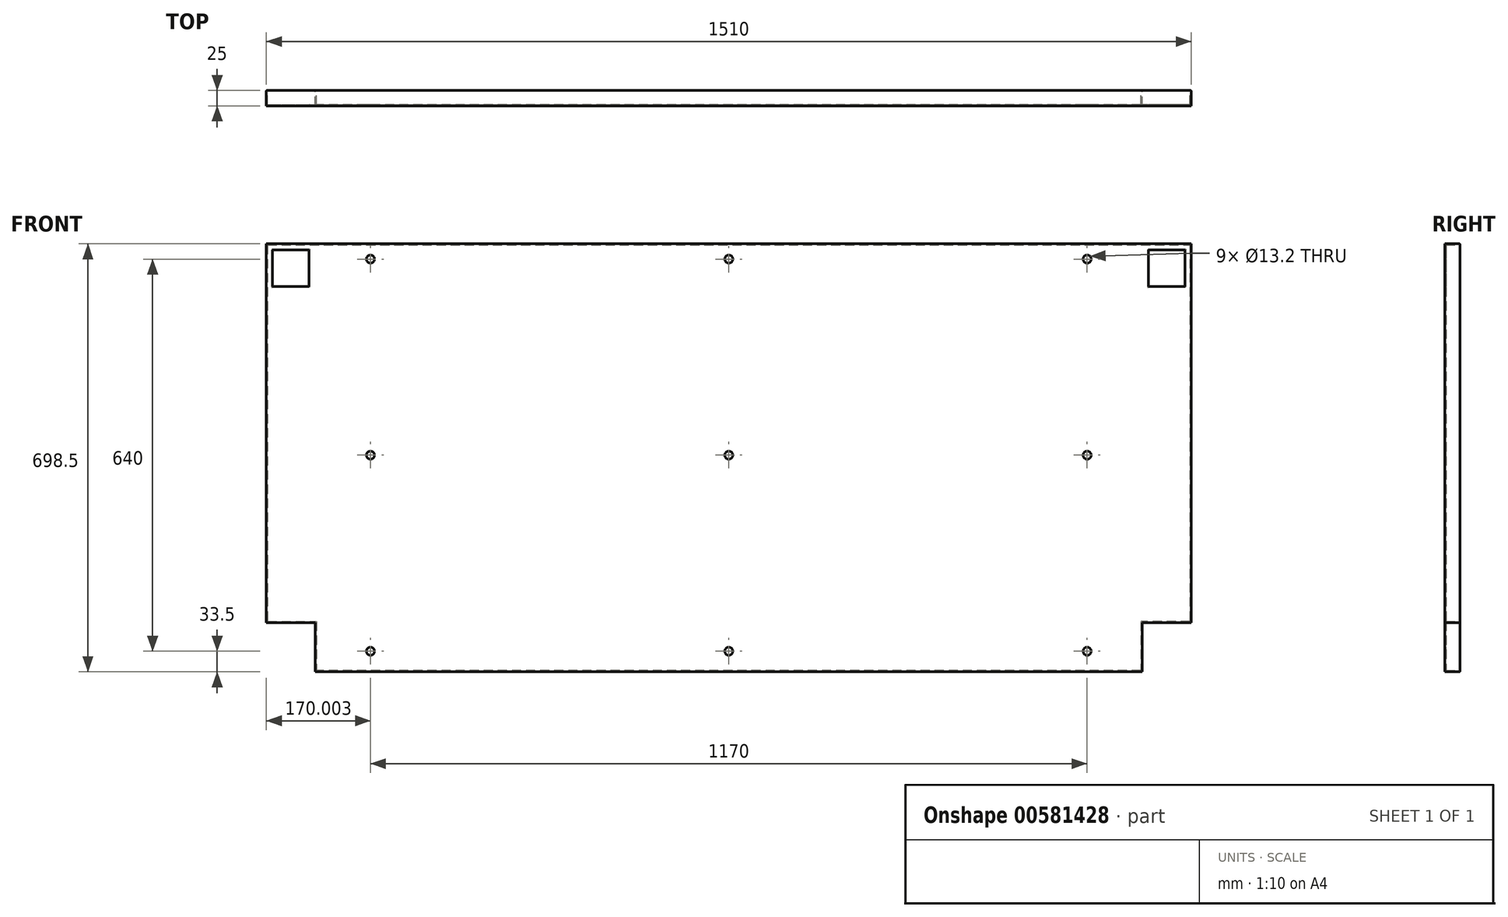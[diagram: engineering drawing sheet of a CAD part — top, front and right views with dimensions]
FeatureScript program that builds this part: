
annotation { "Feature Type Name" : "Feature", "Feature Type Description" : "" }
export const myFeature = defineFeature(function(context is Context, id is Id, definition is map)
    precondition{}
    {
        {
            var Q0;
            Q0=qCreatedBy(makeId("Front.planeOp"),FACE);
            var sketch = newSketch(context, id + "F0", { "sketchPlane" : qUnion([Q0])});
            skLineSegment(sketch, "E0", {"start": v(37.21, 618.5) * mm, "end": v(1547.21, 618.5) * mm});
            skLineSegment(sketch, "E1", {"start": v(37.21, 618.5) * mm, "end": v(37.21, 0) * mm});
            skLineSegment(sketch, "E2", {"start": v(37.21, 0) * mm, "end": v(117.21, 0) * mm});
            skLineSegment(sketch, "E3", {"start": v(117.21, 0) * mm, "end": v(117.21, -80) * mm});
            skLineSegment(sketch, "E4", {"start": v(1547.21, 618.5) * mm, "end": v(1547.21, 0) * mm});
            skLineSegment(sketch, "E5", {"start": v(1547.21, 0) * mm, "end": v(1467.21, 0) * mm});
            skLineSegment(sketch, "E6", {"start": v(1467.21, 0) * mm, "end": v(1467.21, -80) * mm});
            skLineSegment(sketch, "E7", {"start": v(1467.21, -80) * mm, "end": v(117.21, -80) * mm});
            skSolve(sketch);
        }
        {
            var Q0;
            Q0=makeQuery(id+"F0.imprint","IMPRINT",FACE,{"disambiguationData":[TD([[makeQuery(id+"F0.imprint","IMPRINT",EDGE,{"derivedFrom":sQuery(id+"F0.wireOp",EDGE,"E0")}),-1.0]])]});
            extrude(context, id + "F1", {"entities" : qUnion([Q0]), "depth" : 25 * mm, "offsetDistance" : 25 * mm});
        }
        {
            var Q0;
            Q0=makeQuery(id+"F1.opExtrude","CAP_FACE",FACE,{"disambiguationData":[OSD([sQuery(id+"F0.wireOp",EDGE,"E0"),sQuery(id+"F0.wireOp",EDGE,"E1"),sQuery(id+"F0.wireOp",EDGE,"E2"),sQuery(id+"F0.wireOp",EDGE,"E3"),sQuery(id+"F0.wireOp",EDGE,"E4"),sQuery(id+"F0.wireOp",EDGE,"E5"),sQuery(id+"F0.wireOp",EDGE,"E6"),sQuery(id+"F0.wireOp",EDGE,"E7")])],"isStart":true});
            shell(context, id + "F2", {"entities" : qUnion([Q0]), "thickness" : 2 * mm});
        }
        {
            var Q0;
            Q0=makeQuery(id+"F1.opExtrude","CAP_FACE",FACE,{"disambiguationData":[OSD([sQuery(id+"F0.wireOp",EDGE,"E0"),sQuery(id+"F0.wireOp",EDGE,"E1"),sQuery(id+"F0.wireOp",EDGE,"E2"),sQuery(id+"F0.wireOp",EDGE,"E3"),sQuery(id+"F0.wireOp",EDGE,"E4"),sQuery(id+"F0.wireOp",EDGE,"E5"),sQuery(id+"F0.wireOp",EDGE,"E6"),sQuery(id+"F0.wireOp",EDGE,"E7")])],"isStart":false});
            var sketch = newSketch(context, id + "F3", { "sketchPlane" : qUnion([Q0])});
            skLineSegment(sketch, "E8.bottom", {"start": v(37.21, 618.5) * mm, "end": v(47.21, 618.5) * mm});
            skLineSegment(sketch, "E8.top", {"start": v(37.21, 608.5) * mm, "end": v(47.21, 608.5) * mm});
            skLineSegment(sketch, "E8.left", {"start": v(37.21, 618.5) * mm, "end": v(37.21, 608.5) * mm});
            skLineSegment(sketch, "E8.right", {"start": v(47.21, 618.5) * mm, "end": v(47.21, 608.5) * mm});
            skLineSegment(sketch, "E9.bottom", {"start": v(47.21, 608.5) * mm, "end": v(107.21, 608.5) * mm});
            skLineSegment(sketch, "E9.top", {"start": v(47.21, 548.5) * mm, "end": v(107.21, 548.5) * mm});
            skLineSegment(sketch, "E9.left", {"start": v(47.21, 608.5) * mm, "end": v(47.21, 548.5) * mm});
            skLineSegment(sketch, "E9.right", {"start": v(107.21, 608.5) * mm, "end": v(107.21, 548.5) * mm});
            skLineSegment(sketch, "E10.bottom", {"start": v(1547.21, 618.5) * mm, "end": v(1537.21, 618.5) * mm});
            skLineSegment(sketch, "E10.top", {"start": v(1547.21, 608.5) * mm, "end": v(1537.21, 608.5) * mm});
            skLineSegment(sketch, "E10.left", {"start": v(1547.21, 618.5) * mm, "end": v(1547.21, 608.5) * mm});
            skLineSegment(sketch, "E10.right", {"start": v(1537.21, 618.5) * mm, "end": v(1537.21, 608.5) * mm});
            skLineSegment(sketch, "E11.bottom", {"start": v(1537.21, 608.5) * mm, "end": v(1477.21, 608.5) * mm});
            skLineSegment(sketch, "E11.top", {"start": v(1537.21, 548.5) * mm, "end": v(1477.21, 548.5) * mm});
            skLineSegment(sketch, "E11.left", {"start": v(1537.21, 608.5) * mm, "end": v(1537.21, 548.5) * mm});
            skLineSegment(sketch, "E11.right", {"start": v(1477.21, 608.5) * mm, "end": v(1477.21, 548.5) * mm});
            skSolve(sketch);
        }
        {
            var Q0;
            Q0=makeQuery(id+"F3.imprint","IMPRINT",FACE,{"disambiguationData":[TD([[makeQuery(id+"F3.imprint","IMPRINT",EDGE,{"derivedFrom":sQuery(id+"F3.wireOp",EDGE,"E9.bottom")}),-1.0]])]});
            var Q1;
            Q1=makeQuery(id+"F3.imprint","IMPRINT",FACE,{"disambiguationData":[TD([[makeQuery(id+"F3.imprint","IMPRINT",EDGE,{"derivedFrom":sQuery(id+"F3.wireOp",EDGE,"E11.bottom")}),1.0]])]});
            extrude(context, id + "F4", {"entities" : qUnion([Q0, Q1]), "operationType" : NewBodyOperationType.REMOVE, "oppositeDirection" : true, "depth" : 30 * mm, "offsetDistance" : 25 * mm});
        }
        {
            var Q0;
            Q0=makeQuery(id+"F1.opExtrude","CAP_EDGE",EDGE,{"disambiguationData":[OSD([sQuery(id+"F0.wireOp",EDGE,"E0")])],"isStart":true});
            var Q1;
            {var subQ0=sQuery(id+"F0.wireOp",EDGE,"E0");Q1=makeQuery(id+"F2.opShell","OFFSET_EDGE",EDGE,{"disambiguationData":[OSD([subQ0]),TDD([makeQuery(id+"F1.opExtrude","CAP_EDGE",EDGE,{"disambiguationData":[OSD([subQ0])],"isStart":true})])]});}
            var Q2;
            Q2=makeQuery(id+"F1.opExtrude","CAP_EDGE",EDGE,{"disambiguationData":[OSD([sQuery(id+"F0.wireOp",EDGE,"E1")])],"isStart":true});
            var Q3;
            {var subQ0=sQuery(id+"F0.wireOp",EDGE,"E1");Q3=makeQuery(id+"F2.opShell","OFFSET_EDGE",EDGE,{"disambiguationData":[OSD([subQ0]),TDD([makeQuery(id+"F1.opExtrude","CAP_EDGE",EDGE,{"disambiguationData":[OSD([subQ0])],"isStart":true})])]});}
            var Q4;
            {var subQ0=sQuery(id+"F0.wireOp",EDGE,"E2");Q4=makeQuery(id+"F2.opShell","OFFSET_EDGE",EDGE,{"disambiguationData":[OSD([subQ0]),TDD([makeQuery(id+"F1.opExtrude","CAP_EDGE",EDGE,{"disambiguationData":[OSD([subQ0])],"isStart":true})])]});}
            var Q5;
            Q5=makeQuery(id+"F1.opExtrude","CAP_EDGE",EDGE,{"disambiguationData":[OSD([sQuery(id+"F0.wireOp",EDGE,"E2")])],"isStart":true});
            var Q6;
            {var subQ0=sQuery(id+"F0.wireOp",EDGE,"E3");Q6=makeQuery(id+"F2.opShell","OFFSET_EDGE",EDGE,{"disambiguationData":[OSD([subQ0]),TDD([makeQuery(id+"F1.opExtrude","CAP_EDGE",EDGE,{"disambiguationData":[OSD([subQ0])],"isStart":true})])]});}
            var Q7;
            Q7=makeQuery(id+"F1.opExtrude","CAP_EDGE",EDGE,{"disambiguationData":[OSD([sQuery(id+"F0.wireOp",EDGE,"E3")])],"isStart":true});
            var Q8;
            Q8=makeQuery(id+"F1.opExtrude","CAP_EDGE",EDGE,{"disambiguationData":[OSD([sQuery(id+"F0.wireOp",EDGE,"E7")])],"isStart":true});
            var Q9;
            {var subQ0=sQuery(id+"F0.wireOp",EDGE,"E7");Q9=makeQuery(id+"F2.opShell","OFFSET_EDGE",EDGE,{"disambiguationData":[OSD([subQ0]),TDD([makeQuery(id+"F1.opExtrude","CAP_EDGE",EDGE,{"disambiguationData":[OSD([subQ0])],"isStart":true})])]});}
            var Q10;
            Q10=makeQuery(id+"F1.opExtrude","CAP_EDGE",EDGE,{"disambiguationData":[OSD([sQuery(id+"F0.wireOp",EDGE,"E6")])],"isStart":true});
            var Q11;
            {var subQ0=sQuery(id+"F0.wireOp",EDGE,"E6");Q11=makeQuery(id+"F2.opShell","OFFSET_EDGE",EDGE,{"disambiguationData":[OSD([subQ0]),TDD([makeQuery(id+"F1.opExtrude","CAP_EDGE",EDGE,{"disambiguationData":[OSD([subQ0])],"isStart":true})])]});}
            var Q12;
            Q12=makeQuery(id+"F1.opExtrude","CAP_EDGE",EDGE,{"disambiguationData":[OSD([sQuery(id+"F0.wireOp",EDGE,"E5")])],"isStart":true});
            var Q13;
            {var subQ0=sQuery(id+"F0.wireOp",EDGE,"E5");Q13=makeQuery(id+"F2.opShell","OFFSET_EDGE",EDGE,{"disambiguationData":[OSD([subQ0]),TDD([makeQuery(id+"F1.opExtrude","CAP_EDGE",EDGE,{"disambiguationData":[OSD([subQ0])],"isStart":true})])]});}
            var Q14;
            {var subQ0=sQuery(id+"F0.wireOp",EDGE,"E4");Q14=makeQuery(id+"F2.opShell","OFFSET_EDGE",EDGE,{"disambiguationData":[OSD([subQ0]),TDD([makeQuery(id+"F1.opExtrude","CAP_EDGE",EDGE,{"disambiguationData":[OSD([subQ0])],"isStart":true})])]});}
            var Q15;
            Q15=makeQuery(id+"F1.opExtrude","CAP_EDGE",EDGE,{"disambiguationData":[OSD([sQuery(id+"F0.wireOp",EDGE,"E4")])],"isStart":true});
            var Q16;
            Q16=makeQuery(id+"F4.boolean.opBoolean","INTERSECT",EDGE,{"derivedFrom":[makeQuery(id+"F2.opShell","OFFSET_FACE",FACE,{"disambiguationData":[OSD([sQuery(id+"F0.wireOp",EDGE,"E0"),sQuery(id+"F0.wireOp",EDGE,"E1"),sQuery(id+"F0.wireOp",EDGE,"E2"),sQuery(id+"F0.wireOp",EDGE,"E3"),sQuery(id+"F0.wireOp",EDGE,"E4"),sQuery(id+"F0.wireOp",EDGE,"E5"),sQuery(id+"F0.wireOp",EDGE,"E6"),sQuery(id+"F0.wireOp",EDGE,"E7")])]}),makeQuery(id+"F4.opExtrude","SWEPT_FACE",FACE,{"disambiguationData":[OSD([sQuery(id+"F3.wireOp",EDGE,"E11.left")])]})]});
            var Q17;
            Q17=makeQuery(id+"F4.boolean.opBoolean","INTERSECT",EDGE,{"derivedFrom":[makeQuery(id+"F2.opShell","OFFSET_FACE",FACE,{"disambiguationData":[OSD([sQuery(id+"F0.wireOp",EDGE,"E0"),sQuery(id+"F0.wireOp",EDGE,"E1"),sQuery(id+"F0.wireOp",EDGE,"E2"),sQuery(id+"F0.wireOp",EDGE,"E3"),sQuery(id+"F0.wireOp",EDGE,"E4"),sQuery(id+"F0.wireOp",EDGE,"E5"),sQuery(id+"F0.wireOp",EDGE,"E6"),sQuery(id+"F0.wireOp",EDGE,"E7")])]}),makeQuery(id+"F4.opExtrude","SWEPT_FACE",FACE,{"disambiguationData":[OSD([sQuery(id+"F3.wireOp",EDGE,"E11.top")])]})]});
            var Q18;
            Q18=makeQuery(id+"F4.boolean.opBoolean","INTERSECT",EDGE,{"derivedFrom":[makeQuery(id+"F2.opShell","OFFSET_FACE",FACE,{"disambiguationData":[OSD([sQuery(id+"F0.wireOp",EDGE,"E0"),sQuery(id+"F0.wireOp",EDGE,"E1"),sQuery(id+"F0.wireOp",EDGE,"E2"),sQuery(id+"F0.wireOp",EDGE,"E3"),sQuery(id+"F0.wireOp",EDGE,"E4"),sQuery(id+"F0.wireOp",EDGE,"E5"),sQuery(id+"F0.wireOp",EDGE,"E6"),sQuery(id+"F0.wireOp",EDGE,"E7")])]}),makeQuery(id+"F4.opExtrude","SWEPT_FACE",FACE,{"disambiguationData":[OSD([sQuery(id+"F3.wireOp",EDGE,"E11.bottom")])]})]});
            var Q19;
            Q19=makeQuery(id+"F4.boolean.opBoolean","INTERSECT",EDGE,{"derivedFrom":[makeQuery(id+"F2.opShell","OFFSET_FACE",FACE,{"disambiguationData":[OSD([sQuery(id+"F0.wireOp",EDGE,"E0"),sQuery(id+"F0.wireOp",EDGE,"E1"),sQuery(id+"F0.wireOp",EDGE,"E2"),sQuery(id+"F0.wireOp",EDGE,"E3"),sQuery(id+"F0.wireOp",EDGE,"E4"),sQuery(id+"F0.wireOp",EDGE,"E5"),sQuery(id+"F0.wireOp",EDGE,"E6"),sQuery(id+"F0.wireOp",EDGE,"E7")])]}),makeQuery(id+"F4.opExtrude","SWEPT_FACE",FACE,{"disambiguationData":[OSD([sQuery(id+"F3.wireOp",EDGE,"E11.right")])]})]});
            var Q20;
            Q20=makeQuery(id+"F4.boolean.opBoolean","COPY",EDGE,{"derivedFrom":makeQuery(id+"F4.opExtrude","CAP_EDGE",EDGE,{"disambiguationData":[OSD([sQuery(id+"F3.wireOp",EDGE,"E9.left")])],"isStart":true})});
            var Q21;
            Q21=makeQuery(id+"F4.boolean.opBoolean","INTERSECT",EDGE,{"derivedFrom":[makeQuery(id+"F2.opShell","OFFSET_FACE",FACE,{"disambiguationData":[OSD([sQuery(id+"F0.wireOp",EDGE,"E0"),sQuery(id+"F0.wireOp",EDGE,"E1"),sQuery(id+"F0.wireOp",EDGE,"E2"),sQuery(id+"F0.wireOp",EDGE,"E3"),sQuery(id+"F0.wireOp",EDGE,"E4"),sQuery(id+"F0.wireOp",EDGE,"E5"),sQuery(id+"F0.wireOp",EDGE,"E6"),sQuery(id+"F0.wireOp",EDGE,"E7")])]}),makeQuery(id+"F4.opExtrude","SWEPT_FACE",FACE,{"disambiguationData":[OSD([sQuery(id+"F3.wireOp",EDGE,"E9.bottom")])]})]});
            var Q22;
            Q22=makeQuery(id+"F4.boolean.opBoolean","INTERSECT",EDGE,{"derivedFrom":[makeQuery(id+"F2.opShell","OFFSET_FACE",FACE,{"disambiguationData":[OSD([sQuery(id+"F0.wireOp",EDGE,"E0"),sQuery(id+"F0.wireOp",EDGE,"E1"),sQuery(id+"F0.wireOp",EDGE,"E2"),sQuery(id+"F0.wireOp",EDGE,"E3"),sQuery(id+"F0.wireOp",EDGE,"E4"),sQuery(id+"F0.wireOp",EDGE,"E5"),sQuery(id+"F0.wireOp",EDGE,"E6"),sQuery(id+"F0.wireOp",EDGE,"E7")])]}),makeQuery(id+"F4.opExtrude","SWEPT_FACE",FACE,{"disambiguationData":[OSD([sQuery(id+"F3.wireOp",EDGE,"E9.right")])]})]});
            var Q23;
            Q23=makeQuery(id+"F4.boolean.opBoolean","INTERSECT",EDGE,{"derivedFrom":[makeQuery(id+"F2.opShell","OFFSET_FACE",FACE,{"disambiguationData":[OSD([sQuery(id+"F0.wireOp",EDGE,"E0"),sQuery(id+"F0.wireOp",EDGE,"E1"),sQuery(id+"F0.wireOp",EDGE,"E2"),sQuery(id+"F0.wireOp",EDGE,"E3"),sQuery(id+"F0.wireOp",EDGE,"E4"),sQuery(id+"F0.wireOp",EDGE,"E5"),sQuery(id+"F0.wireOp",EDGE,"E6"),sQuery(id+"F0.wireOp",EDGE,"E7")])]}),makeQuery(id+"F4.opExtrude","SWEPT_FACE",FACE,{"disambiguationData":[OSD([sQuery(id+"F3.wireOp",EDGE,"E9.top")])]})]});
            var Q24;
            Q24=makeQuery(id+"F4.boolean.opBoolean","COPY",EDGE,{"derivedFrom":makeQuery(id+"F4.opExtrude","CAP_EDGE",EDGE,{"disambiguationData":[OSD([sQuery(id+"F3.wireOp",EDGE,"E9.top")])],"isStart":true})});
            var Q25;
            Q25=makeQuery(id+"F4.boolean.opBoolean","COPY",EDGE,{"derivedFrom":makeQuery(id+"F4.opExtrude","CAP_EDGE",EDGE,{"disambiguationData":[OSD([sQuery(id+"F3.wireOp",EDGE,"E9.right")])],"isStart":true})});
            var Q26;
            Q26=makeQuery(id+"F4.boolean.opBoolean","INTERSECT",EDGE,{"derivedFrom":[makeQuery(id+"F2.opShell","OFFSET_FACE",FACE,{"disambiguationData":[OSD([sQuery(id+"F0.wireOp",EDGE,"E0"),sQuery(id+"F0.wireOp",EDGE,"E1"),sQuery(id+"F0.wireOp",EDGE,"E2"),sQuery(id+"F0.wireOp",EDGE,"E3"),sQuery(id+"F0.wireOp",EDGE,"E4"),sQuery(id+"F0.wireOp",EDGE,"E5"),sQuery(id+"F0.wireOp",EDGE,"E6"),sQuery(id+"F0.wireOp",EDGE,"E7")])]}),makeQuery(id+"F4.opExtrude","SWEPT_FACE",FACE,{"disambiguationData":[OSD([sQuery(id+"F3.wireOp",EDGE,"E9.left")])]})]});
            var Q27;
            Q27=makeQuery(id+"F4.boolean.opBoolean","COPY",EDGE,{"derivedFrom":makeQuery(id+"F4.opExtrude","CAP_EDGE",EDGE,{"disambiguationData":[OSD([sQuery(id+"F3.wireOp",EDGE,"E9.bottom")])],"isStart":true})});
            var Q28;
            Q28=makeQuery(id+"F4.boolean.opBoolean","COPY",EDGE,{"derivedFrom":makeQuery(id+"F4.opExtrude","CAP_EDGE",EDGE,{"disambiguationData":[OSD([sQuery(id+"F3.wireOp",EDGE,"E11.left")])],"isStart":true})});
            var Q29;
            Q29=makeQuery(id+"F4.boolean.opBoolean","COPY",EDGE,{"derivedFrom":makeQuery(id+"F4.opExtrude","CAP_EDGE",EDGE,{"disambiguationData":[OSD([sQuery(id+"F3.wireOp",EDGE,"E11.bottom")])],"isStart":true})});
            var Q30;
            Q30=makeQuery(id+"F4.boolean.opBoolean","COPY",EDGE,{"derivedFrom":makeQuery(id+"F4.opExtrude","CAP_EDGE",EDGE,{"disambiguationData":[OSD([sQuery(id+"F3.wireOp",EDGE,"E11.top")])],"isStart":true})});
            var Q31;
            Q31=makeQuery(id+"F4.boolean.opBoolean","COPY",EDGE,{"derivedFrom":makeQuery(id+"F4.opExtrude","CAP_EDGE",EDGE,{"disambiguationData":[OSD([sQuery(id+"F3.wireOp",EDGE,"E11.right")])],"isStart":true})});
            fillet(context, id + "F5", {"entities" : qUnion([Q0, Q1, Q2, Q3, Q4, Q5, Q6, Q7, Q8, Q9, Q10, Q11, Q12, Q13, Q14, Q15, Q16, Q17, Q18, Q19, Q20, Q21, Q22, Q23, Q24, Q25, Q26, Q27, Q28, Q29, Q30, Q31]), "radius" : 1 * mm, "tangentPropagation" : true, "allowEdgeOverflow" : false});
        }
        {
            var Q0;
            Q0=makeQuery(id+"F1.opExtrude","CAP_FACE",FACE,{"disambiguationData":[OSD([sQuery(id+"F0.wireOp",EDGE,"E0"),sQuery(id+"F0.wireOp",EDGE,"E1"),sQuery(id+"F0.wireOp",EDGE,"E2"),sQuery(id+"F0.wireOp",EDGE,"E3"),sQuery(id+"F0.wireOp",EDGE,"E4"),sQuery(id+"F0.wireOp",EDGE,"E5"),sQuery(id+"F0.wireOp",EDGE,"E6"),sQuery(id+"F0.wireOp",EDGE,"E7")])],"isStart":false});
            var sketch = newSketch(context, id + "F6", { "sketchPlane" : qUnion([Q0])});
            skCircle(sketch, "E12", {"center": v(207.21, 593.5) * mm, "radius": 9 * mm});
            skCircle(sketch, "E13.0.1.0", {"center": v(207.21, 273.5) * mm, "radius": 9 * mm});
            skCircle(sketch, "E13.0.2.0", {"center": v(207.21, -46.5) * mm, "radius": 9 * mm});
            skCircle(sketch, "E13.1.0.0", {"center": v(792.21, 593.5) * mm, "radius": 9 * mm});
            skCircle(sketch, "E13.1.1.0", {"center": v(792.21, 273.5) * mm, "radius": 9 * mm});
            skCircle(sketch, "E13.1.2.0", {"center": v(792.21, -46.5) * mm, "radius": 9 * mm});
            skCircle(sketch, "E13.2.0.0", {"center": v(1377.21, 593.5) * mm, "radius": 9 * mm});
            skCircle(sketch, "E13.2.1.0", {"center": v(1377.21, 273.5) * mm, "radius": 9 * mm});
            skCircle(sketch, "E13.2.2.0", {"center": v(1377.21, -46.5) * mm, "radius": 9 * mm});
            skLineSegment(sketch, "E13.direction1", {"start": v(207.21, 593.5) * mm, "end": v(792.21, 593.5) * mm, "construction": true});
            skLineSegment(sketch, "E13.direction2", {"start": v(207.21, 593.5) * mm, "end": v(207.21, 273.5) * mm, "construction": true});
            skSolve(sketch);
        }
        {
            var Q0;
            Q0=sQuery(id+"F6.wireOp",VERTEX,"E12.center");
            var Q1;
            Q1=sQuery(id+"F6.wireOp",VERTEX,"E13.0.1.0.center");
            var Q2;
            Q2=sQuery(id+"F6.wireOp",VERTEX,"E13.0.2.0.center");
            var Q3;
            Q3=sQuery(id+"F6.wireOp",VERTEX,"E13.1.2.0.center");
            var Q4;
            Q4=sQuery(id+"F6.wireOp",VERTEX,"E13.1.1.0.center");
            var Q5;
            Q5=sQuery(id+"F6.wireOp",VERTEX,"E13.1.0.0.center");
            var Q6;
            Q6=sQuery(id+"F6.wireOp",VERTEX,"E13.2.0.0.center");
            var Q7;
            Q7=sQuery(id+"F6.wireOp",VERTEX,"E13.2.1.0.center");
            var Q8;
            Q8=sQuery(id+"F6.wireOp",VERTEX,"E13.2.2.0.center");
            var Q9;
            Q9=makeQuery(id+"F1.opExtrude","SWEPT_BODY",BODY,{"disambiguationData":[OSD([sQuery(id+"F0.wireOp",EDGE,"E0"),sQuery(id+"F0.wireOp",EDGE,"E1"),sQuery(id+"F0.wireOp",EDGE,"E2"),sQuery(id+"F0.wireOp",EDGE,"E3"),sQuery(id+"F0.wireOp",EDGE,"E4"),sQuery(id+"F0.wireOp",EDGE,"E5"),sQuery(id+"F0.wireOp",EDGE,"E6"),sQuery(id+"F0.wireOp",EDGE,"E7")])]});
            hole(context, id + "F7", {"style" : HoleStyle.SIMPLE, "endStyle" : HoleEndStyle.THROUGH, "standardTappedOrClearance" : lookupTablePath({ "standard" : "ISO", "fit" : "Normal", "size" : "M12", "type" : "Clearance" }), "standardBlindInLast" : lookupTablePath({ "fit" : "Standard", "standard" : "ISO", "size" : "M12", "type" : "Clearance" }), "holeDiameter" : 13.2 * mm, "majorDiameter" : 5 * mm, "isTappedThrough" : true, "tappedDepth" : 12 * mm, "tapClearance" : 3, "locations" : qUnion([Q0, Q1, Q2, Q3, Q4, Q5, Q6, Q7, Q8]), "scope" : qUnion([Q9])});
        }
    });
